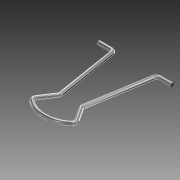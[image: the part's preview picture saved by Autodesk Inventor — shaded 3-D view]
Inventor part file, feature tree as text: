
AUTODESK INVENTOR PART (.ipt)
format: ipt  version: 2013 (Build 170138000, 138)  size: 116,736 bytes
history: native  units: mm
features: sketch x2, sweep x1, mirror x1
ambient origin geometry x8: Origin, YZ Plane, XZ Plane, XY Plane, X Axis, Y Axis, Z Axis, Center Point
bodies: Solid1 (feature_tree)
feature tree (4):
  sweep  "Sweep1"
  mirror  "Mirror1"
  sketch  "Sketch1"  dims[d0=7.0mm d1=6.0mm]
  sketch  "Sketch2"  dims[d2=10.0mm d3=1.5mm d4=37.0mm d5=11.0mm d6=4.0mm d7=1.5mm d9=0.0mm d10=5.0mm]
